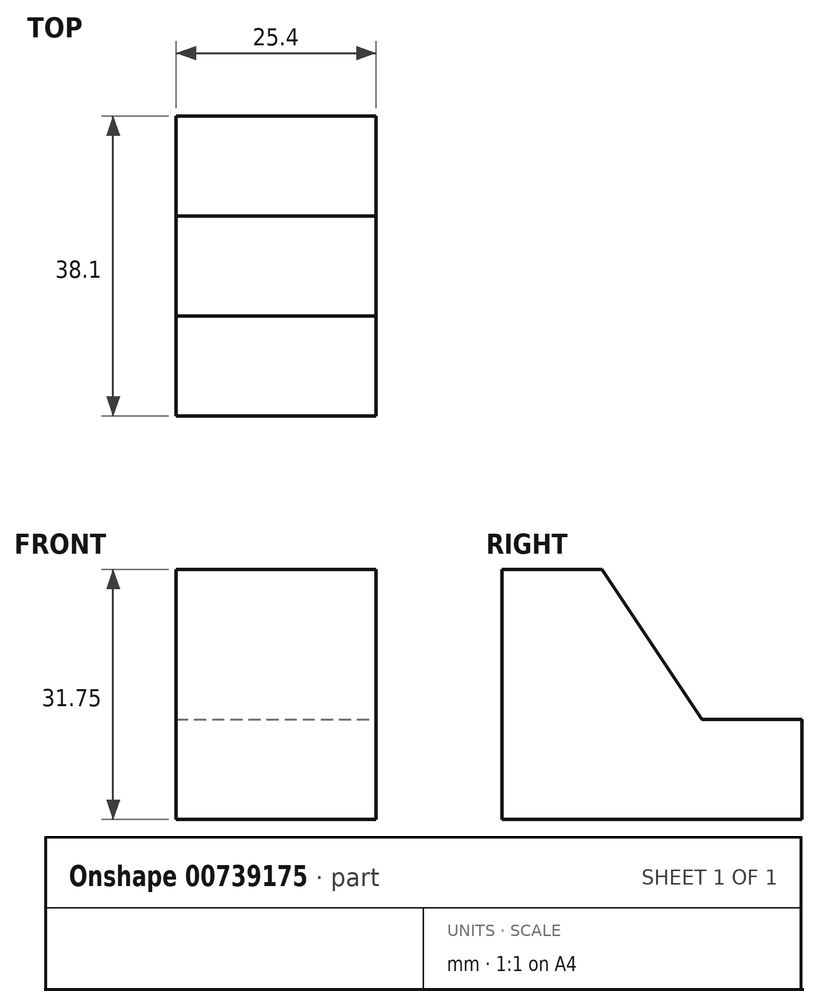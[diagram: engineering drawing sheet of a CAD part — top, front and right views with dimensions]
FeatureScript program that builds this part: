
annotation { "Feature Type Name" : "Feature", "Feature Type Description" : "" }
export const myFeature = defineFeature(function(context is Context, id is Id, definition is map)
    precondition{}
    {
        {
            var Q0;
            Q0=qCreatedBy(makeId("Right.planeOp"),FACE);
            var sketch = newSketch(context, id + "F0", { "sketchPlane" : qUnion([Q0])});
            skLineSegment(sketch, "E0", {"start": v(0, 31.75) * mm, "end": v(0, 0) * mm});
            skLineSegment(sketch, "E1", {"start": v(0, 0) * mm, "end": v(38.1, 0) * mm});
            skLineSegment(sketch, "E2", {"start": v(38.1, 0) * mm, "end": v(38.1, 31.75) * mm});
            skLineSegment(sketch, "E3", {"start": v(38.1, 31.75) * mm, "end": v(0, 31.75) * mm});
            skSolve(sketch);
        }
        {
            var Q0;
            Q0 = qSketchRegion(id + "F0", true);
            var Q1;
            Q1=makeQuery(id+"F0.imprint","IMPRINT",FACE,{"disambiguationData":[TD([[makeQuery(id+"F0.imprint","IMPRINT",EDGE,{"derivedFrom":sQuery(id+"F0.wireOp",EDGE,"E0")}),1.0]])]});
            extrude(context, id + "F1", {"entities" : qUnion([Q0, Q1]), "depth" : 25.4 * mm, "offsetDistance" : 25.4 * mm});
        }
        {
            var Q0;
            Q0=makeQuery(id+"F1.opExtrude","CAP_FACE",FACE,{"disambiguationData":[OSD([sQuery(id+"F0.wireOp",EDGE,"E0"),sQuery(id+"F0.wireOp",EDGE,"E1"),sQuery(id+"F0.wireOp",EDGE,"E2"),sQuery(id+"F0.wireOp",EDGE,"E3")])],"isStart":false});
            var sketch = newSketch(context, id + "F2", { "sketchPlane" : qUnion([Q0])});
            skLineSegment(sketch, "E4", {"start": v(38.1, 12.7) * mm, "end": v(25.4, 12.7) * mm});
            skLineSegment(sketch, "E5", {"start": v(25.4, 12.7) * mm, "end": v(12.7, 31.75) * mm});
            skSolve(sketch);
        }
        {
            var Q0;
            Q0 = qSketchRegion(id + "F2", true);
            var Q1;
            {var subQ0=sQuery(id+"F2.wireOp",EDGE,"E4");Q1=makeQuery(id+"F2.imprint","IMPRINT",FACE,{"disambiguationData":[TD([[makeQuery(id+"F2.imprint","IMPRINT",EDGE,{"derivedFrom":subQ0}),-1.0]])]});}
            extrude(context, id + "F3", {"entities" : qUnion([Q0, Q1]), "operationType" : NewBodyOperationType.REMOVE, "endBound" : BoundingType.THROUGH_ALL, "oppositeDirection" : true, "depth" : 25.4 * mm, "offsetDistance" : 25.4 * mm});
        }
    });
